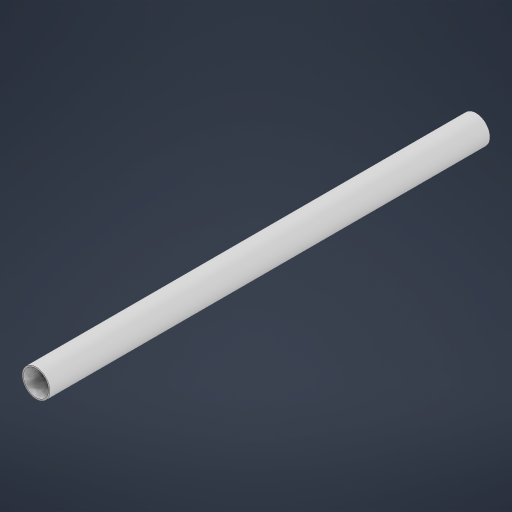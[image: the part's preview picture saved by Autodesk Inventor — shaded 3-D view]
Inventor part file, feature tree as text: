
AUTODESK INVENTOR PART (.ipt)
format: ipt  version: 2024 (Build 280153000, 153)  size: 176,128 bytes
history: native  units: mm
features: extrude x2, sketch x2, other x1
ambient origin geometry x8: Origin, YZ Plane, XZ Plane, XY Plane, X Axis, Y Axis, Z Axis, Center Point
bodies: Body1 (feature_tree)
feature tree (5):
  other  "Sólido1"
  extrude  "Extrusión1"  Depth=3000.0mm TaperAngle=0.0deg
  extrude  "Extrusión3"  Depth=3000.0mm TaperAngle=0.0deg
  sketch  "Boceto1"  dims[d0=190.0mm d1=3000.0mm d2=0.0mm]
  sketch  "Boceto3"  dims[d6=170.62mm d7=3000.0mm d8=0.0mm]
